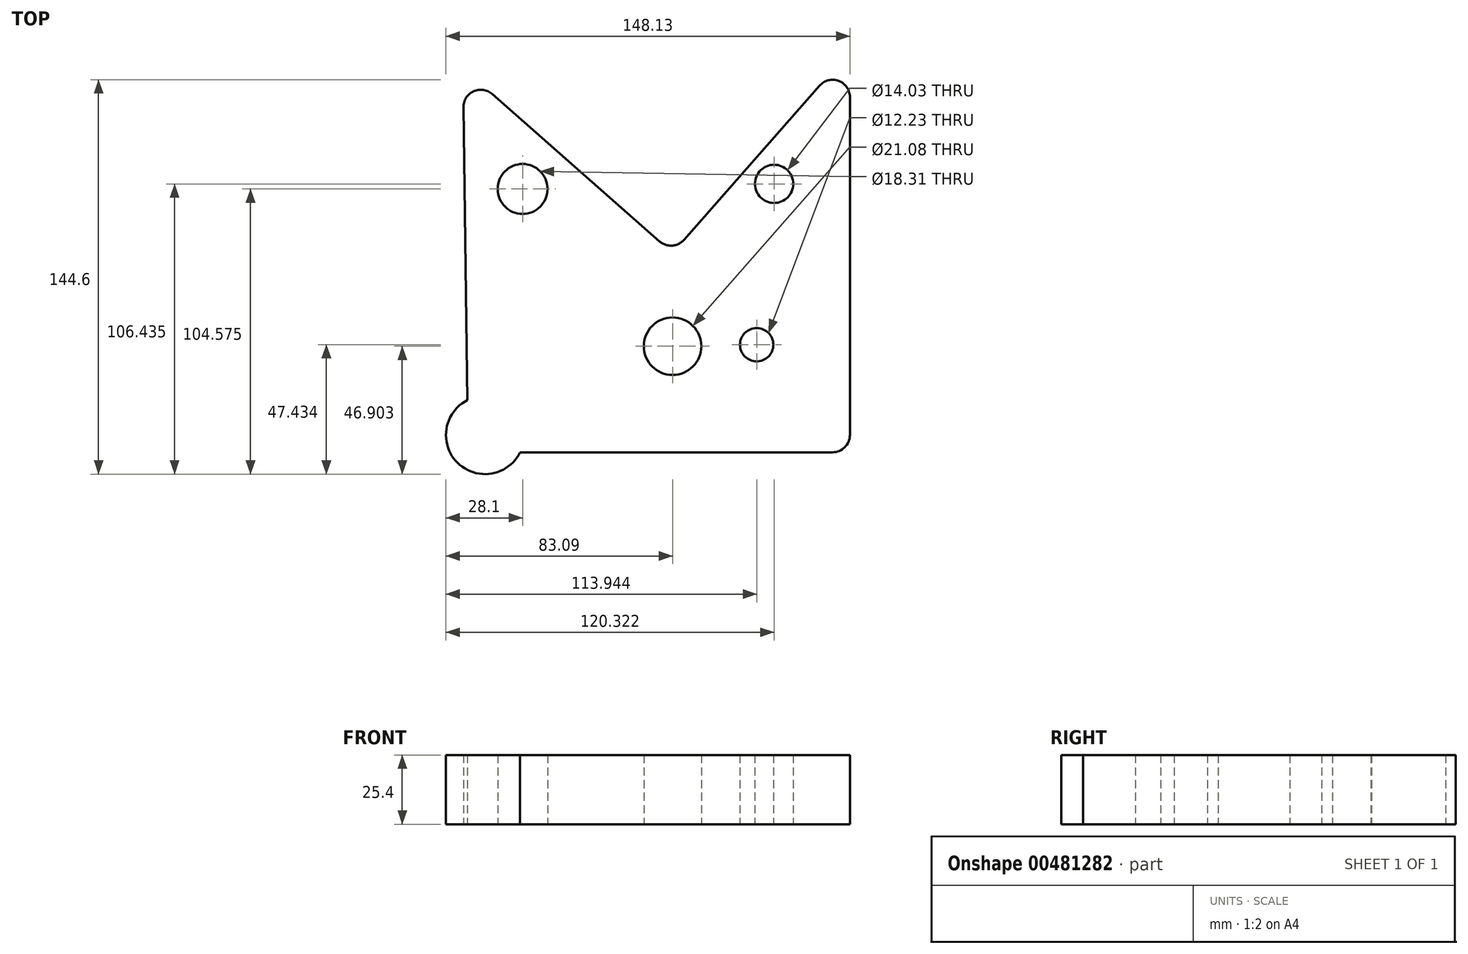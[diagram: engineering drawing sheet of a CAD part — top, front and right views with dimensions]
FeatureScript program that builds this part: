
annotation { "Feature Type Name" : "Feature", "Feature Type Description" : "" }
export const myFeature = defineFeature(function(context is Context, id is Id, definition is map)
    precondition{}
    {
        {
            var Q0;
            Q0=qCreatedBy(makeId("Top.planeOp"),FACE);
            var sketch = newSketch(context, id + "F0", { "sketchPlane" : qUnion([Q0])});
            skLineSegment(sketch, "E0", {"start": v(-66.13, 58.19) * mm, "end": v(-4.77, 4.2) * mm});
            skLineSegment(sketch, "E1", {"start": v(4.2, 4.77) * mm, "end": v(53.92, 61.29) * mm});
            skLineSegment(sketch, "E2", {"start": v(65.04, 57.1) * mm, "end": v(65.04, -66.82) * mm});
            skLineSegment(sketch, "E3", {"start": v(58.69, -73.17) * mm, "end": v(-68.75, -73.17) * mm});
            skLineSegment(sketch, "E4", {"start": v(-75.1, -66.9) * mm, "end": v(-76.68, 53.34) * mm});
            skPoint(sketch, "E5.visualSharp", {"position": v(-76.87, 67.63) * mm});
            skArc(sketch, "E5.filletArc", {"start": v(-66.13, 58.19) * mm, "mid": v(-72.98, 59.19) * mm, "end": v(-76.68, 53.34) * mm});
            skPoint(sketch, "E6.visualSharp", {"position": v(0, 0) * mm});
            skArc(sketch, "E6.filletArc", {"start": v(-4.77, 4.2) * mm, "mid": v(-0.17, 2.62) * mm, "end": v(4.2, 4.77) * mm});
            skPoint(sketch, "E7.visualSharp", {"position": v(65.04, 73.93) * mm});
            skArc(sketch, "E7.filletArc", {"start": v(65.04, 57.1) * mm, "mid": v(60.93, 63.04) * mm, "end": v(53.92, 61.29) * mm});
            skPoint(sketch, "E8.visualSharp", {"position": v(65.04, -73.17) * mm});
            skArc(sketch, "E8.filletArc", {"start": v(58.69, -73.17) * mm, "mid": v(63.18, -71.31) * mm, "end": v(65.04, -66.82) * mm});
            skPoint(sketch, "E9.visualSharp", {"position": v(-75.02, -73.17) * mm});
            skArc(sketch, "E9.filletArc", {"start": v(-75.1, -66.9) * mm, "mid": v(-73.21, -71.34) * mm, "end": v(-68.75, -73.17) * mm});
            skCircle(sketch, "E10", {"center": v(-68.75, -66.82) * mm, "radius": 14.34 * mm});
            skCircle(sketch, "E11", {"center": v(0, -34.26) * mm, "radius": 10.54 * mm});
            skCircle(sketch, "E12", {"center": v(30.85, -33.73) * mm, "radius": 6.11 * mm});
            skCircle(sketch, "E13", {"center": v(37.23, 25.28) * mm, "radius": 7.02 * mm});
            skCircle(sketch, "E14", {"center": v(-54.99, 23.41) * mm, "radius": 9.15 * mm});
            skSolve(sketch);
        }
        {
            var Q0;
            Q0 = qSketchRegion(id + "F0", true);
            extrude(context, id + "F1", {"entities" : qUnion([Q0]), "depth" : 25.4 * mm});
        }
    });
